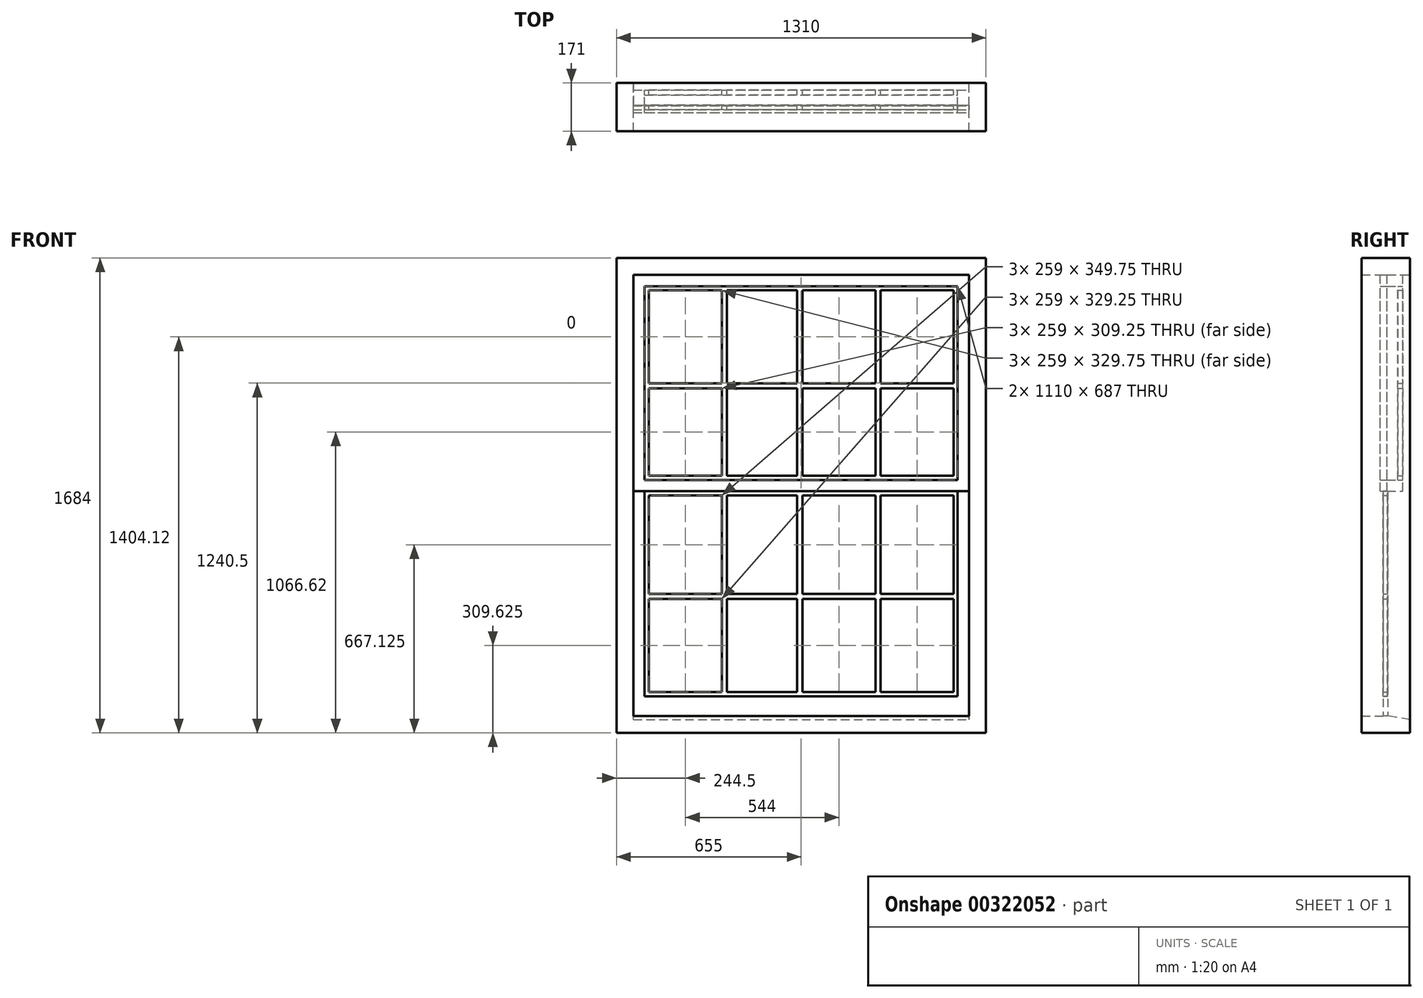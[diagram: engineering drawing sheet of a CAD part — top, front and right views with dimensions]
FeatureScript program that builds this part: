
annotation { "Feature Type Name" : "Feature", "Feature Type Description" : "" }
export const myFeature = defineFeature(function(context is Context, id is Id, definition is map)
    precondition{}
    {
        {
            var Q0;
            Q0=qCreatedBy(makeId("Front.planeOp"),FACE);
            var sketch = newSketch(context, id + "F0", { "sketchPlane" : qUnion([Q0])});
            skLineSegment(sketch, "E0.bottom", {"start": v(0, 0) * mm, "end": v(-1310, 0) * mm});
            skLineSegment(sketch, "E0.top", {"start": v(0, 1684) * mm, "end": v(-1310, 1684) * mm});
            skLineSegment(sketch, "E0.left", {"start": v(0, 0) * mm, "end": v(0, 1684) * mm});
            skLineSegment(sketch, "E0.right", {"start": v(-1310, 0) * mm, "end": v(-1310, 1684) * mm});
            skLineSegment(sketch, "E1.0", {"start": v(-60, 1624) * mm, "end": v(-1250, 1624) * mm});
            skLineSegment(sketch, "E1.1", {"start": v(-60, 60) * mm, "end": v(-60, 1624) * mm});
            skLineSegment(sketch, "E1.2", {"start": v(-60, 60) * mm, "end": v(-1250, 60) * mm});
            skLineSegment(sketch, "E1.3", {"start": v(-1250, 60) * mm, "end": v(-1250, 1624) * mm});
            skLineSegment(sketch, "E2.0", {"start": v(-1210, 130) * mm, "end": v(-1210, 857) * mm});
            skLineSegment(sketch, "E2.1", {"start": v(-100, 1584) * mm, "end": v(-1210, 1584) * mm});
            skLineSegment(sketch, "E2.2", {"start": v(-100, 130) * mm, "end": v(-100, 857) * mm});
            skLineSegment(sketch, "E3.0", {"start": v(-100, 130) * mm, "end": v(-1210, 130) * mm});
            skLineSegment(sketch, "E4", {"start": v(-1250, 857) * mm, "end": v(-60, 857) * mm});
            skLineSegment(sketch, "E5.0", {"start": v(-1210, 897) * mm, "end": v(-100, 897) * mm});
            skPoint(sketch, "E6.orphan", {"position": v(-100, 857) * mm});
            skPoint(sketch, "E7.orphan", {"position": v(-1210, 857) * mm});
            skLineSegment(sketch, "E8.trimOffspring", {"start": v(-100, 897) * mm, "end": v(-100, 1584) * mm});
            skLineSegment(sketch, "E9.trimOffspring", {"start": v(-1210, 897) * mm, "end": v(-1210, 1584) * mm});
            skLineSegment(sketch, "E10.bottom", {"start": v(-115, 1569) * mm, "end": v(-374, 1569) * mm});
            skLineSegment(sketch, "E10.top", {"start": v(-115, 1239.25) * mm, "end": v(-374, 1239.25) * mm});
            skLineSegment(sketch, "E10.left", {"start": v(-115, 1569) * mm, "end": v(-115, 1239.25) * mm});
            skLineSegment(sketch, "E10.right", {"start": v(-918, 1569) * mm, "end": v(-918, 1239.25) * mm});
            skLineSegment(sketch, "E11.bottom", {"start": v(-936, 1569) * mm, "end": v(-1195, 1569) * mm});
            skLineSegment(sketch, "E11.top", {"start": v(-936, 1239.25) * mm, "end": v(-1195, 1239.25) * mm});
            skLineSegment(sketch, "E11.left", {"start": v(-936, 1569) * mm, "end": v(-936, 1239.25) * mm});
            skLineSegment(sketch, "E11.right", {"start": v(-1195, 1569) * mm, "end": v(-1195, 1239.25) * mm});
            skLineSegment(sketch, "E12.bottom", {"start": v(-115, 1221.25) * mm, "end": v(-651, 1221.25) * mm});
            skLineSegment(sketch, "E12.top", {"start": v(-115, 912) * mm, "end": v(-918, 912) * mm});
            skLineSegment(sketch, "E12.left", {"start": v(-115, 1221.25) * mm, "end": v(-115, 912) * mm});
            skLineSegment(sketch, "E12.right", {"start": v(-918, 1221.25) * mm, "end": v(-918, 912) * mm});
            skLineSegment(sketch, "E13.bottom", {"start": v(-936, 1221.25) * mm, "end": v(-1195, 1221.25) * mm});
            skLineSegment(sketch, "E13.top", {"start": v(-936, 912) * mm, "end": v(-1195, 912) * mm});
            skLineSegment(sketch, "E13.left", {"start": v(-936, 1221.25) * mm, "end": v(-936, 912) * mm});
            skLineSegment(sketch, "E13.right", {"start": v(-1195, 1221.25) * mm, "end": v(-1195, 912) * mm});
            skLineSegment(sketch, "E14.bottom", {"start": v(-115, 842) * mm, "end": v(-374, 842) * mm});
            skLineSegment(sketch, "E14.top", {"start": v(-115, 492.25) * mm, "end": v(-374, 492.25) * mm});
            skLineSegment(sketch, "E14.left", {"start": v(-115, 842) * mm, "end": v(-115, 492.25) * mm});
            skLineSegment(sketch, "E14.right", {"start": v(-918, 842) * mm, "end": v(-918, 492.25) * mm});
            skLineSegment(sketch, "E15.bottom", {"start": v(-936, 842) * mm, "end": v(-1195, 842) * mm});
            skLineSegment(sketch, "E15.top", {"start": v(-936, 492.25) * mm, "end": v(-1195, 492.25) * mm});
            skLineSegment(sketch, "E15.left", {"start": v(-936, 842) * mm, "end": v(-936, 492.25) * mm});
            skLineSegment(sketch, "E15.right", {"start": v(-1195, 842) * mm, "end": v(-1195, 492.25) * mm});
            skLineSegment(sketch, "E16.bottom", {"start": v(-115, 474.25) * mm, "end": v(-374, 474.25) * mm});
            skLineSegment(sketch, "E16.top", {"start": v(-115, 145) * mm, "end": v(-374, 145) * mm});
            skLineSegment(sketch, "E16.left", {"start": v(-115, 474.25) * mm, "end": v(-115, 145) * mm});
            skLineSegment(sketch, "E16.right", {"start": v(-918, 474.25) * mm, "end": v(-918, 145) * mm});
            skLineSegment(sketch, "E17.bottom", {"start": v(-936, 474.25) * mm, "end": v(-1195, 474.25) * mm});
            skLineSegment(sketch, "E17.top", {"start": v(-936, 145) * mm, "end": v(-1195, 145) * mm});
            skLineSegment(sketch, "E17.left", {"start": v(-936, 474.25) * mm, "end": v(-936, 145) * mm});
            skLineSegment(sketch, "E17.right", {"start": v(-1195, 474.25) * mm, "end": v(-1195, 145) * mm});
            skLineSegment(sketch, "E18", {"start": v(-374, 1569) * mm, "end": v(-374, 1239.25) * mm});
            skLineSegment(sketch, "E19", {"start": v(-392, 1569) * mm, "end": v(-392, 1239.25) * mm});
            skLineSegment(sketch, "E20.trimOffspring", {"start": v(-392, 1569) * mm, "end": v(-918, 1569) * mm});
            skLineSegment(sketch, "E21.trimOffspring", {"start": v(-392, 1239.25) * mm, "end": v(-651, 1239.25) * mm});
            skLineSegment(sketch, "E22", {"start": v(-374, 1221.25) * mm, "end": v(-374, 912) * mm});
            skLineSegment(sketch, "E23", {"start": v(-392, 1221.25) * mm, "end": v(-392, 912) * mm});
            skLineSegment(sketch, "E24.trimOffspring", {"start": v(-392, 842) * mm, "end": v(-651, 842) * mm});
            skLineSegment(sketch, "E25.trimOffspring", {"start": v(-463.5, 492.25) * mm, "end": v(-651, 492.25) * mm});
            skLineSegment(sketch, "E26.trimOffspring", {"start": v(-467.19, 474.25) * mm, "end": v(-651, 474.25) * mm});
            skLineSegment(sketch, "E27.trimOffspring", {"start": v(-534.5, 145) * mm, "end": v(-651, 145) * mm});
            skLineSegment(sketch, "E28", {"start": v(-651, 1569) * mm, "end": v(-651, 1239.25) * mm});
            skLineSegment(sketch, "E29.0", {"start": v(-669, 1569) * mm, "end": v(-669, 1239.25) * mm});
            skLineSegment(sketch, "E30", {"start": v(-651, 842) * mm, "end": v(-651, 492.25) * mm});
            skPoint(sketch, "E31.orphan", {"position": v(-374, 842) * mm});
            skLineSegment(sketch, "E32", {"start": v(-374, 842) * mm, "end": v(-374, 492.25) * mm});
            skLineSegment(sketch, "E33", {"start": v(-392, 842) * mm, "end": v(-392, 492.25) * mm});
            skLineSegment(sketch, "E34", {"start": v(-669, 842) * mm, "end": v(-669, 492.25) * mm});
            skPoint(sketch, "E34.startSnap0", {"position": v(-655, 842) * mm});
            skLineSegment(sketch, "E35.trimOffspring", {"start": v(-669, 474.25) * mm, "end": v(-669, 145) * mm});
            skLineSegment(sketch, "E36.trimOffspring", {"start": v(-669, 492.25) * mm, "end": v(-918, 492.25) * mm});
            skLineSegment(sketch, "E37.trimOffspring", {"start": v(-651, 474.25) * mm, "end": v(-651, 145) * mm});
            skLineSegment(sketch, "E38.trimOffspring", {"start": v(-669, 474.25) * mm, "end": v(-918, 474.25) * mm});
            skLineSegment(sketch, "E39.trimOffspring", {"start": v(-392, 492.25) * mm, "end": v(-463.5, 492.25) * mm});
            skLineSegment(sketch, "E40.trimOffspring", {"start": v(-392, 474.25) * mm, "end": v(-392, 145) * mm});
            skLineSegment(sketch, "E41.trimOffspring", {"start": v(-374, 474.25) * mm, "end": v(-374, 145) * mm});
            skLineSegment(sketch, "E42.trimOffspring", {"start": v(-392, 474.25) * mm, "end": v(-467.19, 474.25) * mm});
            skLineSegment(sketch, "E43.trimOffspring", {"start": v(-669, 842) * mm, "end": v(-918, 842) * mm});
            skLineSegment(sketch, "E44.trimOffspring", {"start": v(-392, 145) * mm, "end": v(-534.5, 145) * mm});
            skLineSegment(sketch, "E45.trimOffspring", {"start": v(-669, 145) * mm, "end": v(-918, 145) * mm});
            skLineSegment(sketch, "E46.trimOffspring", {"start": v(-669, 1239.25) * mm, "end": v(-918, 1239.25) * mm});
            skLineSegment(sketch, "E47.trimOffspring", {"start": v(-669, 1221.25) * mm, "end": v(-669, 912) * mm});
            skLineSegment(sketch, "E48.trimOffspring", {"start": v(-669, 1221.25) * mm, "end": v(-918, 1221.25) * mm});
            skLineSegment(sketch, "E49.trimOffspring", {"start": v(-651, 1221.25) * mm, "end": v(-651, 912) * mm});
            skSolve(sketch);
        }
        {
            var Q0;
            Q0=makeQuery(id+"F0.imprint","IMPRINT",FACE,{"disambiguationData":[TD([[makeQuery(id+"F0.imprint","IMPRINT",EDGE,{"derivedFrom":sQuery(id+"F0.wireOp",EDGE,"E0.bottom")}),-1.0]])]});
            extrude(context, id + "F1", {"entities" : qUnion([Q0]), "depth" : 146 * mm, "hasSecondDirection" : true, "secondDirectionOppositeDirection" : true, "secondDirectionDepth" : 25 * mm});
        }
        {
            var Q0;
            {var subQ1=sQuery(id+"F0.wireOp",EDGE,"E1.0");Q0=makeQuery(id+"F0.imprint","IMPRINT",FACE,{"disambiguationData":[TD([[makeQuery(id+"F0.imprint","IMPRINT",EDGE,{"derivedFrom":subQ1}),1.0]])]});}
            extrude(context, id + "F2", {"entities" : qUnion([Q0]), "depth" : 56 * mm});
        }
        {
            var Q0;
            Q0=makeQuery(id+"F0.imprint","IMPRINT",FACE,{"disambiguationData":[TD([[makeQuery(id+"F0.imprint","IMPRINT",EDGE,{"derivedFrom":sQuery(id+"F0.wireOp",EDGE,"E2.1")}),1.0]])]});
            var Q1;
            {var subQ0=sQuery(id+"F0.wireOp",EDGE,"E22");Q1=makeQuery(id+"F0.imprint","IMPRINT",FACE,{"disambiguationData":[TD([[makeQuery(id+"F0.imprint","IMPRINT",EDGE,{"derivedFrom":subQ0}),-1.0]])]});}
            extrude(context, id + "F3", {"entities" : qUnion([Q0, Q1]), "depth" : 18 * mm, "hasSecondDirection" : true, "secondDirectionOppositeDirection" : false, "secondDirectionDepth" : 1 * mm});
        }
        {
            var Q0;
            Q0=makeQuery(id+"FIrM3R81E3h49M7_4.imprint","IMPRINT",FACE,{"disambiguationData":[TD([[makeQuery(id+"FIrM3R81E3h49M7_4.imprint","IMPRINT",EDGE,{"derivedFrom":sQuery(id+"FIrM3R81E3h49M7_4.wireOp",EDGE,"avv4JBCt-yASB-qjdQ-SY2H-WYt19sHGvwVq.bottom")}),-1.0]])]});
            var Q1;
            {var subQ1=sQuery(id+"F0.wireOp",EDGE,"E2.0");Q1=makeQuery(id+"F0.imprint","IMPRINT",FACE,{"disambiguationData":[TD([[makeQuery(id+"F0.imprint","IMPRINT",EDGE,{"derivedFrom":subQ1}),-1.0]])]});}
            extrude(context, id + "F4", {"entities" : qUnion([Q0, Q1]), "depth" : 70 * mm, "hasSecondDirection" : true, "secondDirectionOppositeDirection" : false, "secondDirectionDepth" : 55 * mm});
        }
        {
            var Q0;
            Q0=makeQuery(id+"F1.opExtrude","CAP_EDGE",EDGE,{"disambiguationData":[OSD([sQuery(id+"F0.wireOp",EDGE,"E1.2")])],"isStart":true});
            chamfer(context, id + "F5", {"entities" : qUnion([Q0]), "chamferType" : ChamferType.OFFSET_ANGLE, "width" : 80 * mm, "oppositeDirection" : false, "angle" : 9 * degree, "tangentPropagation" : true});
        }
        {
            var Q0;
            Q0=makeQuery(id+"F2.opExtrude","CAP_FACE",FACE,{"disambiguationData":[OSD([sQuery(id+"F0.wireOp",EDGE,"E1.0"),sQuery(id+"F0.wireOp",EDGE,"E1.1"),sQuery(id+"F0.wireOp",EDGE,"E1.3"),sQuery(id+"F0.wireOp",EDGE,"E2.1"),sQuery(id+"F0.wireOp",EDGE,"E4"),sQuery(id+"F0.wireOp",EDGE,"E5.0"),sQuery(id+"F0.wireOp",EDGE,"E8.trimOffspring"),sQuery(id+"F0.wireOp",EDGE,"E9.trimOffspring")])],"isStart":false});
            extrude(context, id + "F6", {"entities" : qUnion([Q0]), "depth" : 25 * mm});
        }
        {
            var Q0;
            Q0=makeQuery(id+"F4.opExtrude","CAP_FACE",FACE,{"disambiguationData":[OSD([sQuery(id+"F0.wireOp",EDGE,"E2.0"),sQuery(id+"F0.wireOp",EDGE,"E2.2"),sQuery(id+"F0.wireOp",EDGE,"E3.0"),sQuery(id+"F0.wireOp",EDGE,"E4"),sQuery(id+"F0.wireOp",EDGE,"E14.bottom"),sQuery(id+"F0.wireOp",EDGE,"E14.top"),sQuery(id+"F0.wireOp",EDGE,"E14.left"),sQuery(id+"F0.wireOp",EDGE,"E14.right"),sQuery(id+"F0.wireOp",EDGE,"E15.bottom"),sQuery(id+"F0.wireOp",EDGE,"E15.top"),sQuery(id+"F0.wireOp",EDGE,"E15.left"),sQuery(id+"F0.wireOp",EDGE,"E15.right"),sQuery(id+"F0.wireOp",EDGE,"E16.bottom"),sQuery(id+"F0.wireOp",EDGE,"E16.top"),sQuery(id+"F0.wireOp",EDGE,"E16.left"),sQuery(id+"F0.wireOp",EDGE,"E16.right"),sQuery(id+"F0.wireOp",EDGE,"E17.bottom"),sQuery(id+"F0.wireOp",EDGE,"E17.top"),sQuery(id+"F0.wireOp",EDGE,"E17.left"),sQuery(id+"F0.wireOp",EDGE,"E17.right"),sQuery(id+"F0.wireOp",EDGE,"E24.trimOffspring"),sQuery(id+"F0.wireOp",EDGE,"E25.trimOffspring"),sQuery(id+"F0.wireOp",EDGE,"E26.trimOffspring"),sQuery(id+"F0.wireOp",EDGE,"E27.trimOffspring"),sQuery(id+"F0.wireOp",EDGE,"E30"),sQuery(id+"F0.wireOp",EDGE,"E32"),sQuery(id+"F0.wireOp",EDGE,"E33"),sQuery(id+"F0.wireOp",EDGE,"E34"),sQuery(id+"F0.wireOp",EDGE,"E35.trimOffspring"),sQuery(id+"F0.wireOp",EDGE,"E36.trimOffspring"),sQuery(id+"F0.wireOp",EDGE,"E37.trimOffspring"),sQuery(id+"F0.wireOp",EDGE,"E38.trimOffspring"),sQuery(id+"F0.wireOp",EDGE,"E39.trimOffspring"),sQuery(id+"F0.wireOp",EDGE,"E40.trimOffspring"),sQuery(id+"F0.wireOp",EDGE,"E41.trimOffspring"),sQuery(id+"F0.wireOp",EDGE,"E42.trimOffspring"),sQuery(id+"F0.wireOp",EDGE,"E43.trimOffspring"),sQuery(id+"F0.wireOp",EDGE,"E44.trimOffspring"),sQuery(id+"F0.wireOp",EDGE,"E45.trimOffspring")])],"isStart":false});
            var sketch = newSketch(context, id + "F7", { "sketchPlane" : qUnion([Q0])});
            skLineSegment(sketch, "E50.bottom", {"start": v(-1250.97, 857) * mm, "end": v(-60, 857) * mm});
            skLineSegment(sketch, "E50.top", {"start": v(-1250.97, 60) * mm, "end": v(-60, 60) * mm});
            skLineSegment(sketch, "E50.left", {"start": v(-1250.97, 857) * mm, "end": v(-1250.97, 60) * mm});
            skLineSegment(sketch, "E50.right", {"start": v(-60, 857) * mm, "end": v(-60, 60) * mm});
            skSolve(sketch);
        }
        {
            var Q0;
            Q0=makeQuery(id+"F7.imprint","IMPRINT",FACE,{"disambiguationData":[TD([[makeQuery(id+"F7.imprint","IMPRINT",EDGE,{"derivedFrom":sQuery(id+"F7.wireOp",EDGE,"E50.top")}),1.0]])]});
            extrude(context, id + "F8", {"entities" : qUnion([Q0]), "oppositeDirection" : true, "depth" : 16 * mm});
        }
    });
